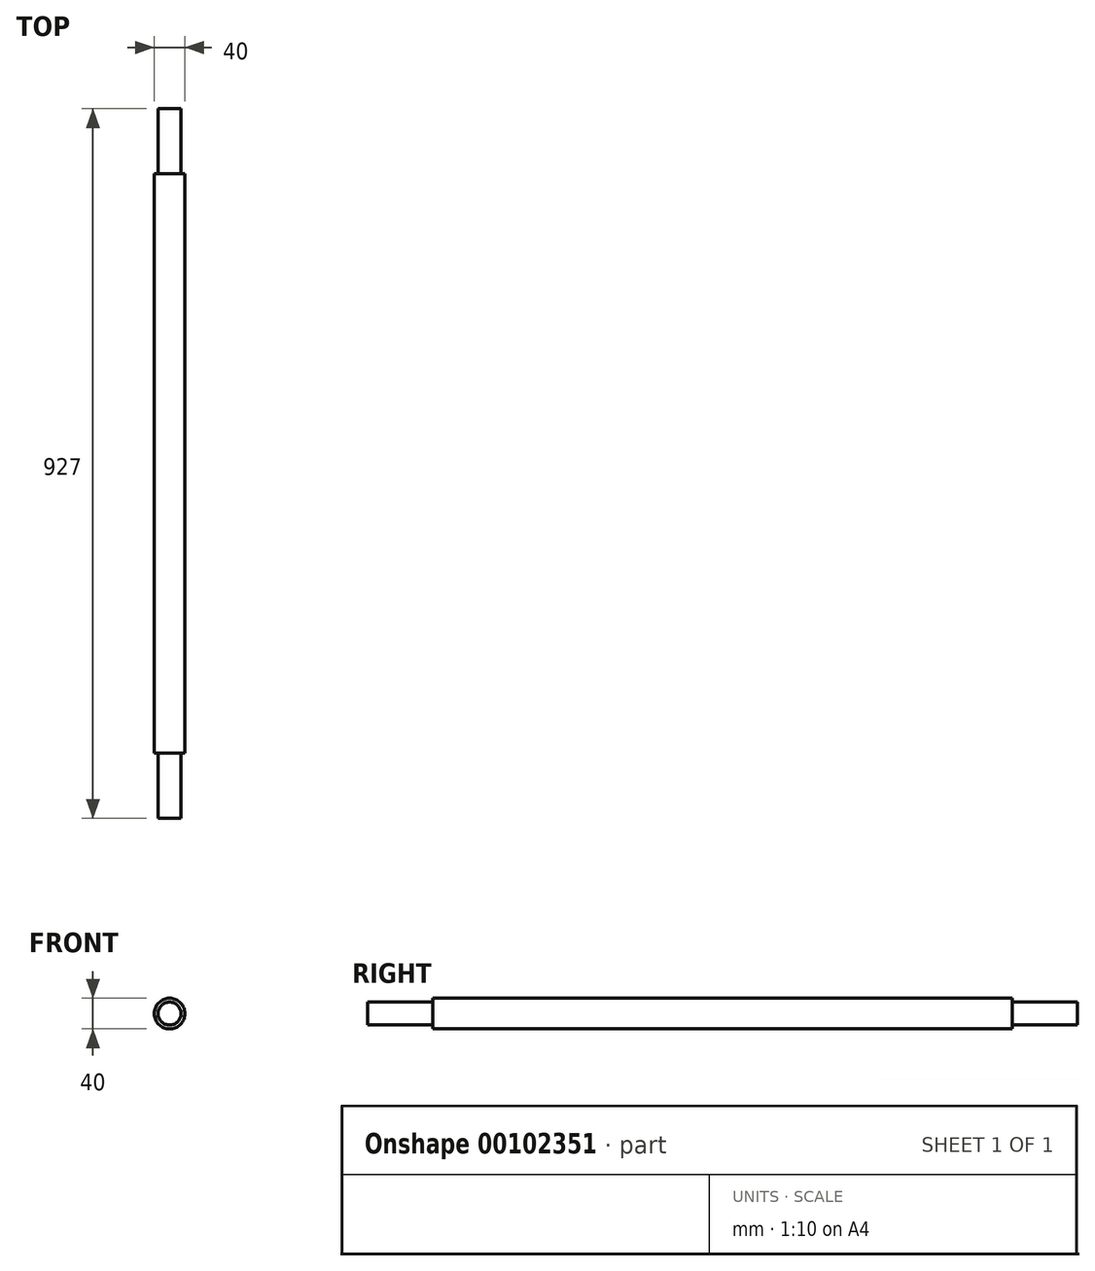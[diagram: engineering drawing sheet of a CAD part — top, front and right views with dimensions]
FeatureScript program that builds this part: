
annotation { "Feature Type Name" : "Feature", "Feature Type Description" : "" }
export const myFeature = defineFeature(function(context is Context, id is Id, definition is map)
    precondition{}
    {
        {
            var Q0;
            Q0=qCreatedBy(makeId("Front.planeOp"),FACE);
            var sketch = newSketch(context, id + "F0", { "sketchPlane" : qUnion([Q0])});
            skCircle(sketch, "E0", {"center": v(0, 0) * mm, "radius": 20 * mm});
            skSolve(sketch);
        }
        {
            var Q0;
            Q0=makeQuery(id+"F0.imprint","IMPRINT",FACE,{"disambiguationData":[TD([[makeQuery(id+"F0.imprint","IMPRINT",EDGE,{"derivedFrom":sQuery(id+"F0.wireOp",EDGE,"E0")}),1.0]])]});
            extrude(context, id + "F1", {"entities" : qUnion([Q0]), "oppositeDirection" : true, "depth" : 757 * mm, "offsetDistance" : 25 * mm});
        }
        {
            var Q0;
            Q0=makeQuery(id+"F0.imprint","IMPRINT",FACE,{"disambiguationData":[TD([[makeQuery(id+"F0.imprint","IMPRINT",EDGE,{"derivedFrom":sQuery(id+"F0.wireOp",EDGE,"E0")}),1.0]])]});
            var sketch = newSketch(context, id + "F2", { "sketchPlane" : qUnion([Q0])});
            skCircle(sketch, "E1", {"center": v(0, 0) * mm, "radius": 15 * mm});
            skSolve(sketch);
        }
        {
            var Q0;
            Q0=makeQuery(id+"F1.opExtrude","CAP_FACE",FACE,{"disambiguationData":[OSD([sQuery(id+"F0.wireOp",EDGE,"E0")])],"isStart":false});
            var sketch = newSketch(context, id + "F3", { "sketchPlane" : qUnion([Q0])});
            skCircle(sketch, "E2", {"center": v(0, 0) * mm, "radius": 15 * mm});
            skSolve(sketch);
        }
        {
            var Q0;
            Q0=makeQuery(id+"F2.imprint","IMPRINT",FACE,{"disambiguationData":[TD([[makeQuery(id+"F2.imprint","IMPRINT",EDGE,{"derivedFrom":sQuery(id+"F2.wireOp",EDGE,"E1")}),1.0]])]});
            extrude(context, id + "F4", {"entities" : qUnion([Q0]), "operationType" : NewBodyOperationType.ADD, "depth" : 85 * mm, "offsetDistance" : 25 * mm});
        }
        {
            var Q0;
            Q0=makeQuery(id+"F3.imprint","IMPRINT",FACE,{"disambiguationData":[TD([[makeQuery(id+"F3.imprint","IMPRINT",EDGE,{"derivedFrom":sQuery(id+"F3.wireOp",EDGE,"E2")}),1.0]])]});
            extrude(context, id + "F5", {"entities" : qUnion([Q0]), "operationType" : NewBodyOperationType.ADD, "depth" : 85 * mm, "offsetDistance" : 25 * mm});
        }
    });
